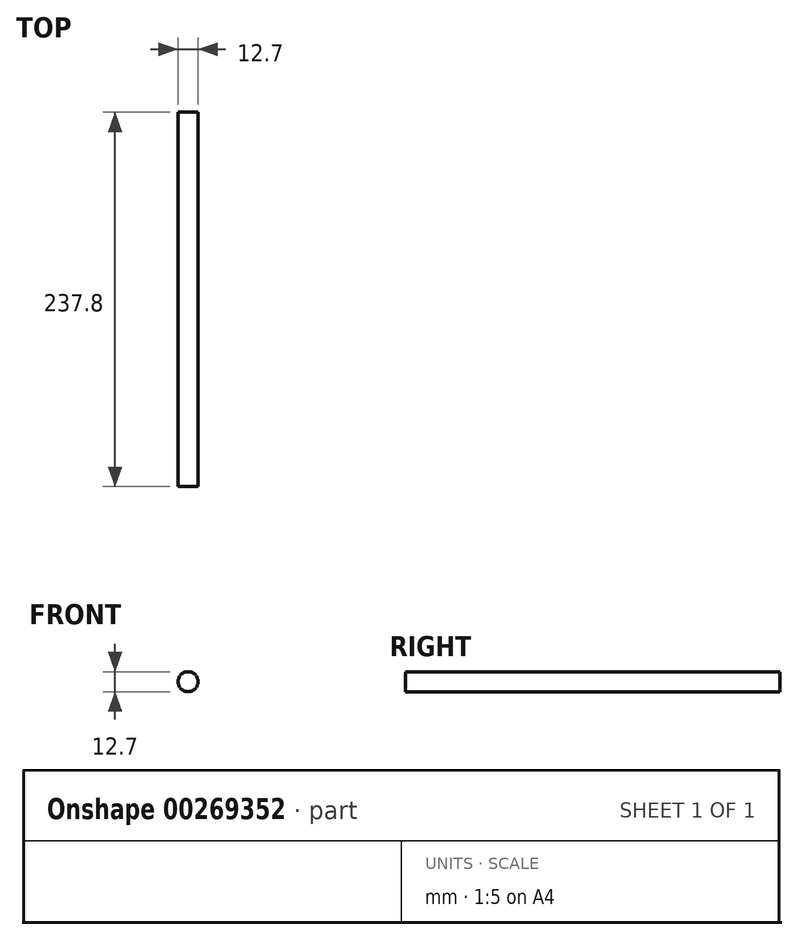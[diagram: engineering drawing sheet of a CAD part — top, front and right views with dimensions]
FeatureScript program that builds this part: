
annotation { "Feature Type Name" : "Feature", "Feature Type Description" : "" }
export const myFeature = defineFeature(function(context is Context, id is Id, definition is map)
    precondition{}
    {
        {
            var Q0;
            Q0=qCreatedBy(makeId("Front.planeOp"),FACE);
            var sketch = newSketch(context, id + "F0", { "sketchPlane" : qUnion([Q0])});
            skCircle(sketch, "E0", {"center": v(0, 0) * mm, "radius": 6.35 * mm});
            skSolve(sketch);
        }
        {
            var Q0;
            Q0 = qSketchRegion(id + "F0", true);
            extrude(context, id + "F1", {"entities" : qUnion([Q0]), "depth" : 237.8 * mm});
        }
    });
